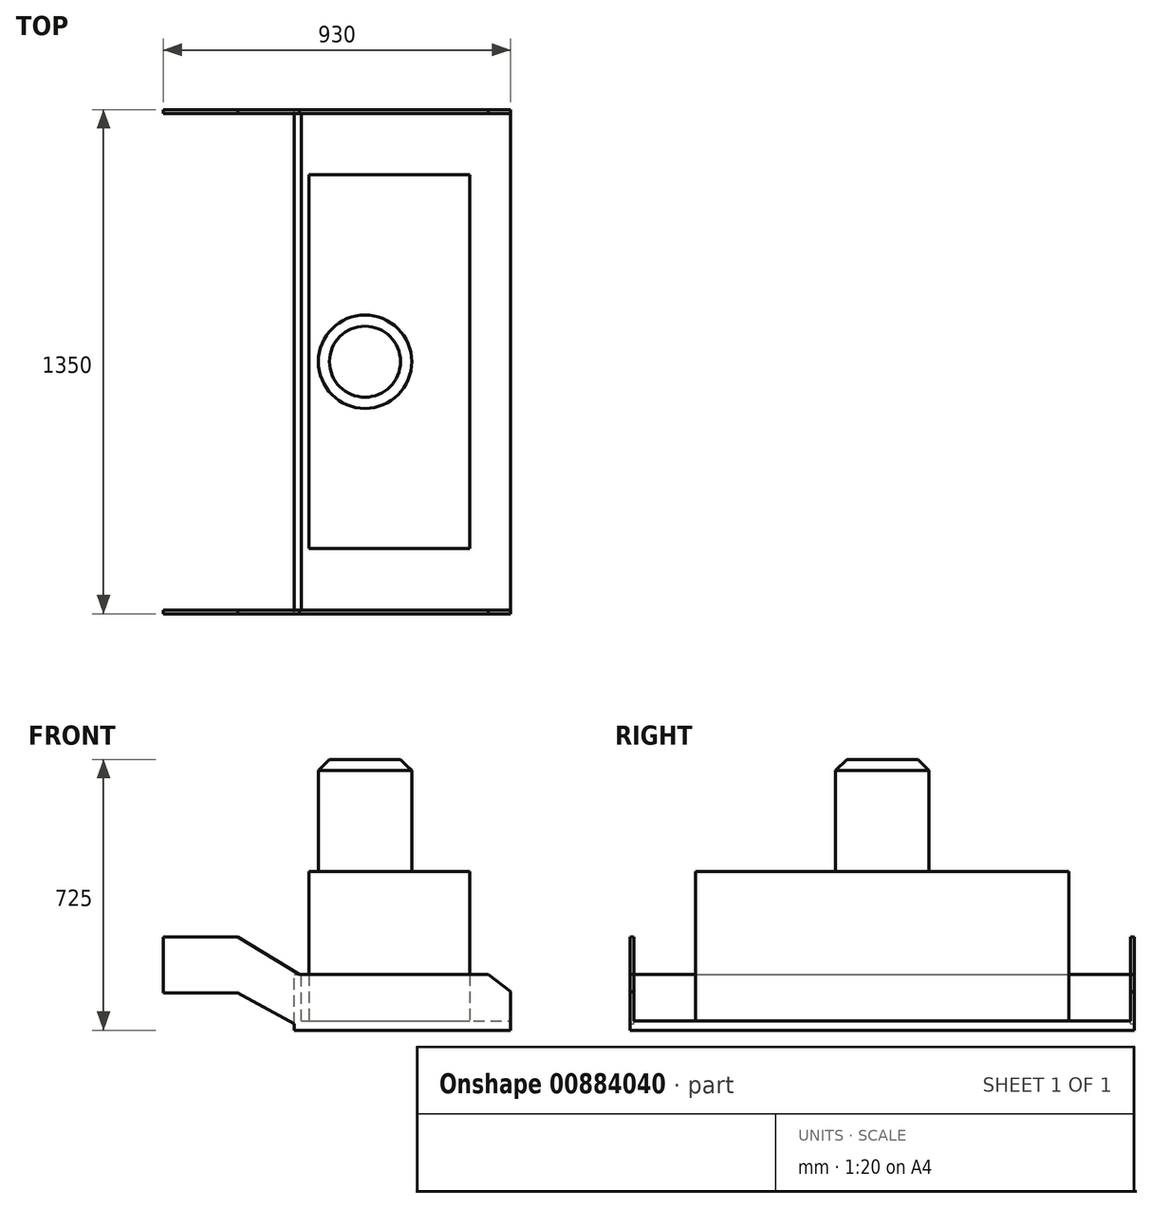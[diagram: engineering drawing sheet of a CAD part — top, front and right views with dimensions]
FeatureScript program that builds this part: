
annotation { "Feature Type Name" : "Feature", "Feature Type Description" : "" }
export const myFeature = defineFeature(function(context is Context, id is Id, definition is map)
    precondition{}
    {
        {
            var Q0;
            Q0=qCreatedBy(makeId("Front.planeOp"),FACE);
            var sketch = newSketch(context, id + "F0", { "sketchPlane" : qUnion([Q0])});
            skLineSegment(sketch, "E0.bottom", {"start": v(0, 250) * mm, "end": v(200, 250) * mm});
            skLineSegment(sketch, "E0.top", {"start": v(0, 100) * mm, "end": v(200, 100) * mm});
            skLineSegment(sketch, "E0.left", {"start": v(0, 250) * mm, "end": v(0, 100) * mm});
            skLineSegment(sketch, "E0.right", {"start": v(200, 250) * mm, "end": v(200, 100) * mm});
            skLineSegment(sketch, "E1.bottom", {"start": v(350, 0) * mm, "end": v(930, 0) * mm});
            skLineSegment(sketch, "E1.top", {"start": v(364.7, 150) * mm, "end": v(869.5, 150) * mm});
            skLineSegment(sketch, "E1.left", {"start": v(350, 0) * mm, "end": v(350, 17.27) * mm});
            skLineSegment(sketch, "E1.right", {"start": v(930, 0) * mm, "end": v(930, 103.2) * mm});
            skLineSegment(sketch, "E2", {"start": v(200, 100) * mm, "end": v(350, 17.27) * mm});
            skLineSegment(sketch, "E3", {"start": v(200, 250) * mm, "end": v(364.7, 150) * mm});
            skLineSegment(sketch, "E4", {"start": v(869.5, 150) * mm, "end": v(930, 103.2) * mm});
            skSolve(sketch);
        }
        {
            var Q0;
            Q0=qSketchRegion(id+"F0",true);
            extrude(context, id + "F1", {"entities" : qUnion([Q0]), "depth" : 10 * mm, "offsetDistance" : 25 * mm});
        }
        {
            var Q0;
            Q0=makeQuery(id+"F1.opExtrude","CAP_FACE",FACE,{"disambiguationData":[OSD([sQuery(id+"F0.wireOp",EDGE,"E0.bottom"),sQuery(id+"F0.wireOp",EDGE,"E0.top"),sQuery(id+"F0.wireOp",EDGE,"E0.left"),sQuery(id+"F0.wireOp",EDGE,"E1.bottom"),sQuery(id+"F0.wireOp",EDGE,"E1.top"),sQuery(id+"F0.wireOp",EDGE,"E1.left"),sQuery(id+"F0.wireOp",EDGE,"E1.right"),sQuery(id+"F0.wireOp",EDGE,"E2"),sQuery(id+"F0.wireOp",EDGE,"E3"),sQuery(id+"F0.wireOp",EDGE,"E4")])],"isStart":false});
            var sketch = newSketch(context, id + "F2", { "sketchPlane" : qUnion([Q0])});
            skLineSegment(sketch, "E5.bottom", {"start": v(350, 0) * mm, "end": v(930, 0) * mm});
            skLineSegment(sketch, "E5.top", {"start": v(350, 25) * mm, "end": v(930, 25) * mm});
            skLineSegment(sketch, "E5.left", {"start": v(350, 0) * mm, "end": v(350, 25) * mm});
            skLineSegment(sketch, "E5.right", {"start": v(930, 0) * mm, "end": v(930, 25) * mm});
            skLineSegment(sketch, "E6.bottom", {"start": v(350, 25) * mm, "end": v(370, 25) * mm});
            skLineSegment(sketch, "E6.top", {"start": v(350, 150) * mm, "end": v(370, 150) * mm});
            skLineSegment(sketch, "E6.left", {"start": v(350, 25) * mm, "end": v(350, 150) * mm});
            skLineSegment(sketch, "E6.right", {"start": v(370, 25) * mm, "end": v(370, 150) * mm});
            skSolve(sketch);
        }
        {
            var Q0;
            Q0=qSketchRegion(id+"F2",true);
            extrude(context, id + "F3", {"entities" : qUnion([Q0]), "operationType" : NewBodyOperationType.ADD, "depth" : 1330 * mm, "offsetDistance" : 25 * mm});
        }
        {
            var Q0;
            Q0=makeQuery(id+"F3.opExtrude","CAP_FACE",FACE,{"disambiguationData":[OSD([sQuery(id+"F2.wireOp",EDGE,"E5.bottom"),sQuery(id+"F2.wireOp",EDGE,"E5.top"),sQuery(id+"F2.wireOp",EDGE,"E5.left"),sQuery(id+"F2.wireOp",EDGE,"E5.right"),sQuery(id+"F2.wireOp",EDGE,"E6.top"),sQuery(id+"F2.wireOp",EDGE,"E6.left"),sQuery(id+"F2.wireOp",EDGE,"E6.right")])],"isStart":false});
            var sketch = newSketch(context, id + "F4", { "sketchPlane" : qUnion([Q0])});
            skPoint(sketch, "E7.0", {"position": v(0, 175) * mm});
            skLineSegment(sketch, "E8.0", {"start": v(0, 250) * mm, "end": v(0, 100) * mm});
            skLineSegment(sketch, "E9.0", {"start": v(0, 250) * mm, "end": v(200, 250) * mm});
            skLineSegment(sketch, "E10.0", {"start": v(200, 250) * mm, "end": v(364.7, 150) * mm});
            skLineSegment(sketch, "E11.0", {"start": v(0, 100) * mm, "end": v(200, 100) * mm});
            skLineSegment(sketch, "E12.0", {"start": v(200, 100) * mm, "end": v(350, 17.27) * mm});
            skLineSegment(sketch, "E13.0", {"start": v(370, 150) * mm, "end": v(869.5, 150) * mm});
            skPoint(sketch, "E14.0", {"position": v(899.75, 126.6) * mm});
            skLineSegment(sketch, "E15.0", {"start": v(869.5, 150) * mm, "end": v(930, 103.2) * mm});
            skLineSegment(sketch, "E16.0", {"start": v(930, 25) * mm, "end": v(930, 103.2) * mm});
            skLineSegment(sketch, "E17.0", {"start": v(930, 0) * mm, "end": v(930, 25) * mm});
            skLineSegment(sketch, "E18.0", {"start": v(350, 0) * mm, "end": v(930, 0) * mm});
            skLineSegment(sketch, "E19.0", {"start": v(350, 0) * mm, "end": v(350, 150) * mm});
            skSolve(sketch);
        }
        {
            var Q0;
            Q0=makeQuery(id+"F4.imprint","IMPRINT",FACE,{"disambiguationData":[TD([[makeQuery(id+"F4.imprint","IMPRINT",EDGE,{"derivedFrom":sQuery(id+"F4.wireOp",EDGE,"E8.0")}),1.0]])]});
            var Q1;
            Q1=makeQuery(id+"F4.imprint","IMPRINT",FACE,{"disambiguationData":[TD([[makeQuery(id+"F4.imprint","IMPRINT",EDGE,{"derivedFrom":sQuery(id+"F4.wireOp",EDGE,"E17.0")}),1.0]])]});
            var Q2;
            Q2=makeQuery(id+"F4.imprint","IMPRINT",FACE,{"disambiguationData":[TD([[makeQuery(id+"F4.imprint","IMPRINT",EDGE,{"derivedFrom":sQuery(id+"F4.wireOp",EDGE,"E13.0")}),-1.0]])]});
            extrude(context, id + "F5", {"entities" : qUnion([Q0, Q1, Q2]), "operationType" : NewBodyOperationType.ADD, "depth" : 10 * mm, "offsetDistance" : 25 * mm});
        }
        {
            var Q0;
            Q0=makeQuery(id+"F3.opExtrude","SWEPT_FACE",FACE,{"disambiguationData":[OSD([sQuery(id+"F2.wireOp",EDGE,"E5.top")])]});
            var sketch = newSketch(context, id + "F6", { "sketchPlane" : qUnion([Q0])});
            skLineSegment(sketch, "E20.bottom", {"start": v(390, -1175) * mm, "end": v(820, -1175) * mm});
            skLineSegment(sketch, "E20.top", {"start": v(390, -175) * mm, "end": v(820, -175) * mm});
            skLineSegment(sketch, "E20.left", {"start": v(390, -1175) * mm, "end": v(390, -175) * mm});
            skLineSegment(sketch, "E20.right", {"start": v(820, -1175) * mm, "end": v(820, -175) * mm});
            skSolve(sketch);
        }
        {
            var Q0;
            Q0=makeQuery(id+"F6.imprint","IMPRINT",FACE,{"disambiguationData":[TD([[makeQuery(id+"F6.imprint","IMPRINT",EDGE,{"derivedFrom":sQuery(id+"F6.wireOp",EDGE,"E20.bottom")}),1.0]])]});
            extrude(context, id + "F7", {"entities" : qUnion([Q0]), "depth" : 400 * mm, "offsetDistance" : 25 * mm});
        }
        {
            var Q0;
            Q0=makeQuery(id+"F7.opExtrude","CAP_FACE",FACE,{"disambiguationData":[OSD([sQuery(id+"F6.wireOp",EDGE,"E20.bottom"),sQuery(id+"F6.wireOp",EDGE,"E20.top"),sQuery(id+"F6.wireOp",EDGE,"E20.left"),sQuery(id+"F6.wireOp",EDGE,"E20.right")])],"isStart":false});
            var sketch = newSketch(context, id + "F8", { "sketchPlane" : qUnion([Q0])});
            skCircle(sketch, "E21", {"center": v(540, -675) * mm, "radius": 125 * mm});
            skSolve(sketch);
        }
        {
            var Q0;
            Q0=makeQuery(id+"F8.imprint","IMPRINT",FACE,{"disambiguationData":[TD([[makeQuery(id+"F8.imprint","IMPRINT",EDGE,{"derivedFrom":sQuery(id+"F8.wireOp",EDGE,"E21")}),1.0]])]});
            extrude(context, id + "F9", {"entities" : qUnion([Q0]), "operationType" : NewBodyOperationType.ADD, "depth" : 300 * mm, "offsetDistance" : 25 * mm});
        }
        {
            var Q0;
            Q0=makeQuery(id+"F9.opExtrude","CAP_EDGE",EDGE,{"disambiguationData":[OSD([sQuery(id+"F8.wireOp",EDGE,"E21")])],"isStart":false});
            chamfer(context, id + "F10", {"entities" : qUnion([Q0]), "width" : 30 * mm, "tangentPropagation" : true});
        }
    });
